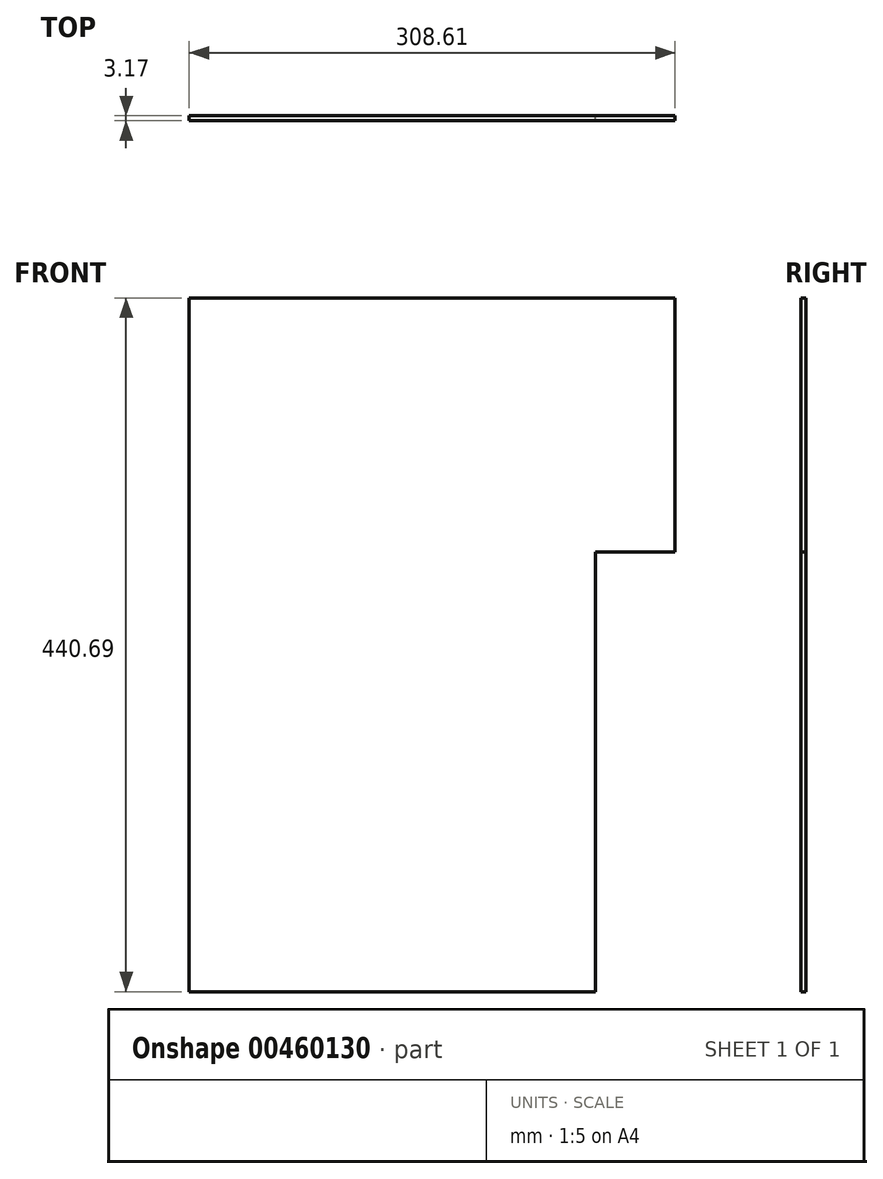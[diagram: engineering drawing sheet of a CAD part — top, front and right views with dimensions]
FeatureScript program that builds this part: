
annotation { "Feature Type Name" : "Feature", "Feature Type Description" : "" }
export const myFeature = defineFeature(function(context is Context, id is Id, definition is map)
    precondition{}
    {
        {
            var Q0;
            Q0=qCreatedBy(makeId("Front.planeOp"),FACE);
            var sketch = newSketch(context, id + "F0", { "sketchPlane" : qUnion([Q0])});
            skLineSegment(sketch, "E0", {"start": v(0, 0) * mm, "end": v(0, 440.7) * mm});
            skLineSegment(sketch, "E1", {"start": v(0, 440.7) * mm, "end": v(308.61, 440.7) * mm});
            skLineSegment(sketch, "E2", {"start": v(308.61, 440.7) * mm, "end": v(308.61, 279.4) * mm});
            skLineSegment(sketch, "E3", {"start": v(308.61, 279.4) * mm, "end": v(257.81, 279.4) * mm});
            skLineSegment(sketch, "E4", {"start": v(257.81, 279.4) * mm, "end": v(257.81, 0) * mm});
            skLineSegment(sketch, "E5", {"start": v(257.81, 0) * mm, "end": v(0, 0) * mm});
            skSolve(sketch);
        }
        {
            var Q0;
            Q0=makeQuery(id+"F0.imprint","IMPRINT",FACE,{"disambiguationData":[TD([[makeQuery(id+"F0.imprint","IMPRINT",EDGE,{"derivedFrom":sQuery(id+"F0.wireOp",EDGE,"E0")}),-1.0]])]});
            extrude(context, id + "F1", {"entities" : qUnion([Q0]), "depth" : 3.17 * mm});
        }
    });
